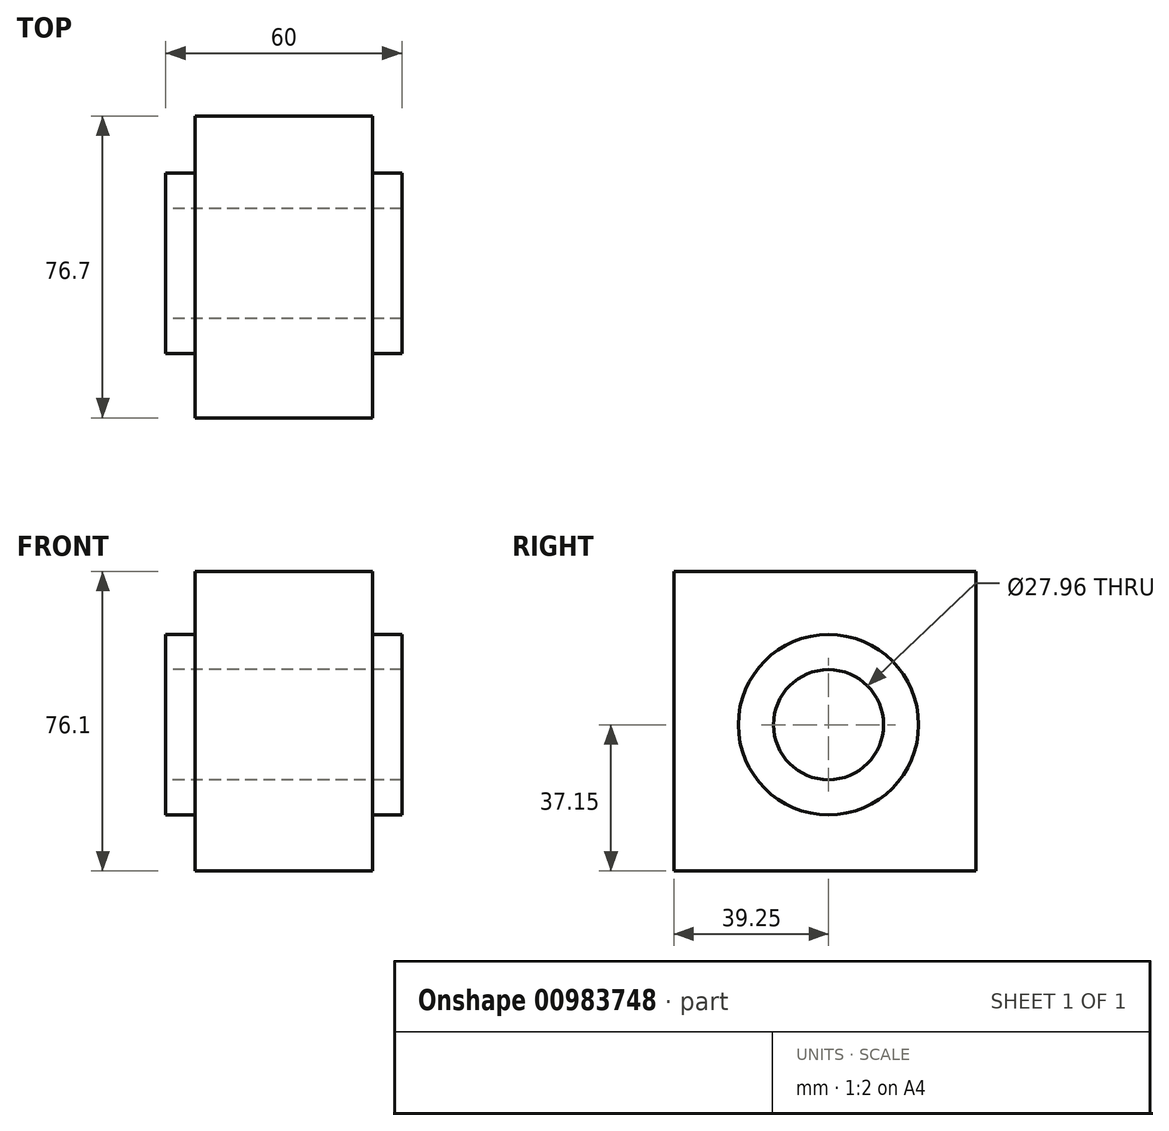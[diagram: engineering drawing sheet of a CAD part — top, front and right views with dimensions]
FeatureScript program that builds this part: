
annotation { "Feature Type Name" : "Feature", "Feature Type Description" : "" }
export const myFeature = defineFeature(function(context is Context, id is Id, definition is map)
    precondition{}
    {
        {
            var Q0;
            Q0=qCreatedBy(makeId("Right.planeOp"),FACE);
            var sketch = newSketch(context, id + "F0", { "sketchPlane" : qUnion([Q0])});
            skCircle(sketch, "E0", {"center": v(0, 0) * mm, "radius": 13.98 * mm});
            skCircle(sketch, "E1", {"center": v(0, 0) * mm, "radius": 22.9 * mm});
            skSolve(sketch);
        }
        {
            var Q0;
            Q0 = qSketchRegion(id + "F0", true);
            extrude(context, id + "F1", {"entities" : qUnion([Q0]), "endBound" : BoundingType.SYMMETRIC, "depth" : 60 * mm, "offsetDistance" : 25.4 * mm});
        }
        {
            var Q0;
            Q0=qCreatedBy(makeId("Right.planeOp"),FACE);
            var sketch = newSketch(context, id + "F2", { "sketchPlane" : qUnion([Q0])});
            skLineSegment(sketch, "E2", {"start": v(0, 38.95) * mm, "end": v(37.45, 38.95) * mm});
            skLineSegment(sketch, "E3", {"start": v(37.45, 38.95) * mm, "end": v(37.45, -37.15) * mm});
            skLineSegment(sketch, "E4", {"start": v(37.45, -37.15) * mm, "end": v(-39.25, -37.15) * mm});
            skLineSegment(sketch, "E5", {"start": v(-39.25, -37.15) * mm, "end": v(-39.25, 38.95) * mm});
            skLineSegment(sketch, "E6", {"start": v(-39.25, 38.95) * mm, "end": v(0, 38.95) * mm});
            skSolve(sketch);
        }
        {
            var Q0;
            Q0 = qSketchRegion(id + "F2", true);
            extrude(context, id + "F3", {"entities" : qUnion([Q0]), "operationType" : NewBodyOperationType.ADD, "endBound" : BoundingType.SYMMETRIC, "depth" : 45 * mm, "offsetDistance" : 25.4 * mm});
        }
        {
            var Q0;
            Q0=makeQuery(id+"F3.boolean.opBoolean","SPLIT",FACE,{"disambiguationData":[TD([makeQuery(id+"F1.opExtrude","SWEPT_FACE",FACE,{"disambiguationData":[OSD([sQuery(id+"F0.wireOp",EDGE,"E0")])]})])],"derivedFrom":makeQuery(id+"F3.opExtrude","CAP_FACE",FACE,{"disambiguationData":[OSD([sQuery(id+"F2.wireOp",EDGE,"E2"),sQuery(id+"F2.wireOp",EDGE,"E3"),sQuery(id+"F2.wireOp",EDGE,"E4"),sQuery(id+"F2.wireOp",EDGE,"E5"),sQuery(id+"F2.wireOp",EDGE,"E6")])],"isStart":true})});
            var sketch = newSketch(context, id + "F4", { "sketchPlane" : qUnion([Q0])});
            skCircle(sketch, "E7", {"center": v(0, 0) * mm, "radius": 14.28 * mm});
            skSolve(sketch);
        }
        {
            var Q0;
            Q0=makeQuery(id+"F4.imprint","IMPRINT",FACE,{"disambiguationData":[TD([[makeQuery(id+"F4.imprint","IMPRINT",EDGE,{"derivedFrom":makeQuery(id+"F3.boolean.opBoolean","INTERSECT",EDGE,{"derivedFrom":[makeQuery(id+"F1.opExtrude","SWEPT_FACE",FACE,{"disambiguationData":[OSD([sQuery(id+"F0.wireOp",EDGE,"E0")])]}),makeQuery(id+"F3.opExtrude","CAP_FACE",FACE,{"disambiguationData":[OSD([sQuery(id+"F2.wireOp",EDGE,"E2"),sQuery(id+"F2.wireOp",EDGE,"E3"),sQuery(id+"F2.wireOp",EDGE,"E4"),sQuery(id+"F2.wireOp",EDGE,"E5"),sQuery(id+"F2.wireOp",EDGE,"E6")])],"isStart":true})]})}),-1.0]])]});
            extrude(context, id + "F5", {"entities" : qUnion([Q0]), "operationType" : NewBodyOperationType.REMOVE, "endBound" : BoundingType.THROUGH_ALL, "oppositeDirection" : true, "depth" : 65 * mm, "offsetDistance" : 25 * mm});
        }
    });
